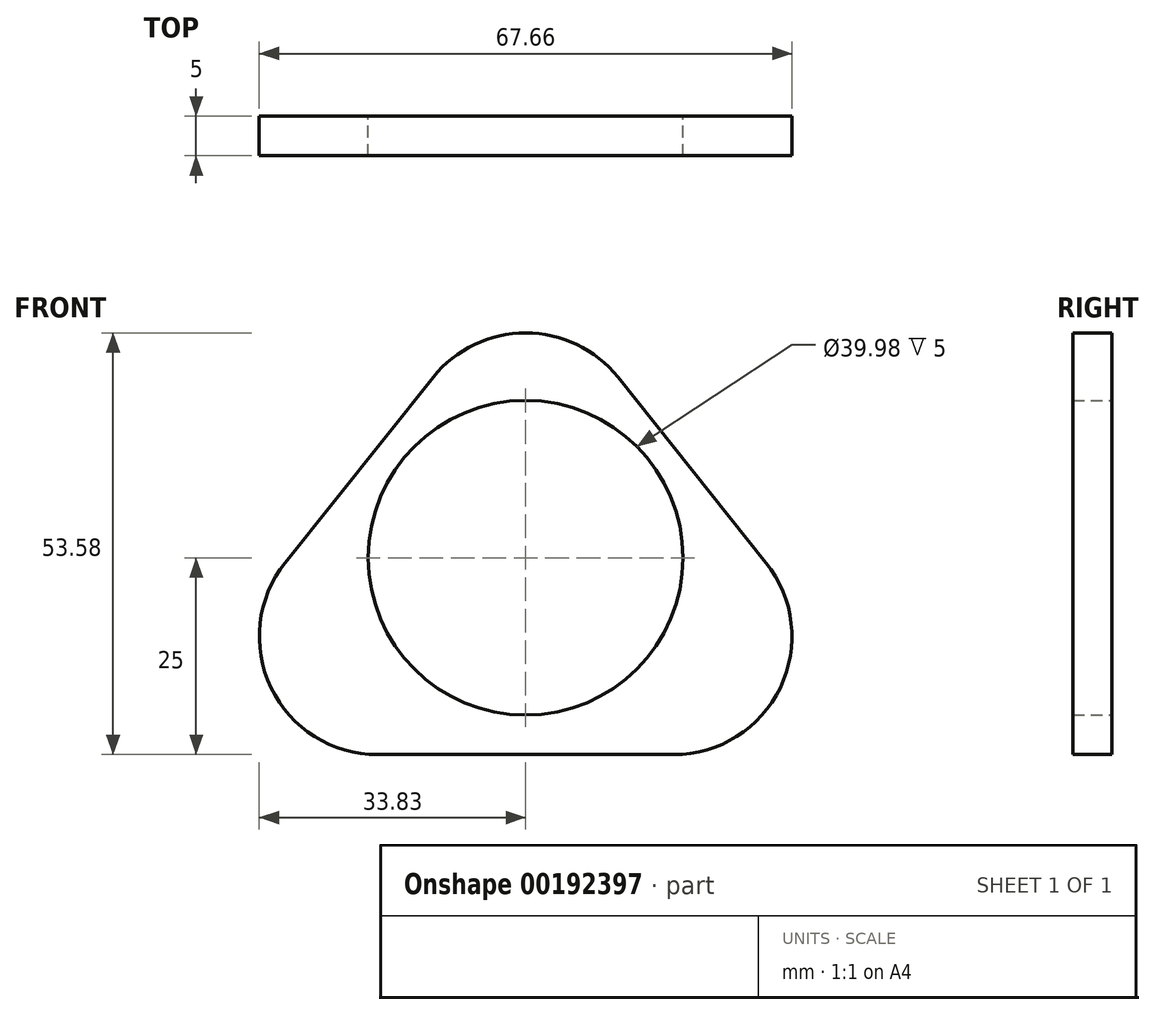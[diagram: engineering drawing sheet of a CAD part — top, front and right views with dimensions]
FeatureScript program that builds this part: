
annotation { "Feature Type Name" : "Feature", "Feature Type Description" : "" }
export const myFeature = defineFeature(function(context is Context, id is Id, definition is map)
    precondition{}
    {
        {
            var Q0;
            Q0=qCreatedBy(makeId("Front.planeOp"),FACE);
            var sketch = newSketch(context, id + "F0", { "sketchPlane" : qUnion([Q0])});
            skCircle(sketch, "E0", {"center": v(0, 0) * mm, "radius": 19.99 * mm});
            skLineSegment(sketch, "E1", {"start": v(0, -25) * mm, "end": v(-50, -25) * mm});
            skLineSegment(sketch, "E2", {"start": v(-50, -25) * mm, "end": v(0, 37.62) * mm});
            skLineSegment(sketch, "E3.MirrorCS", {"start": v(50, -25) * mm, "end": v(0, 37.62) * mm});
            skLineSegment(sketch, "E4.MirrorCS", {"start": v(0, -25) * mm, "end": v(50, -25) * mm});
            skSolve(sketch);
        }
        {
            var Q0;
            Q0 = qSketchRegion(id + "F0", true);
            extrude(context, id + "F1", {"entities" : qUnion([Q0]), "depth" : 5 * mm});
        }
        {
            var Q0;
            Q0=makeQuery(id+"F1.opExtrude","SWEPT_EDGE",EDGE,{"disambiguationData":[OSD([sQuery(id+"F0.wireOp",EDGE,"E2"),sQuery(id+"F0.wireOp",EDGE,"E3.MirrorCS")])]});
            var Q1;
            Q1=makeQuery(id+"F1.opExtrude","SWEPT_EDGE",EDGE,{"disambiguationData":[OSD([sQuery(id+"F0.wireOp",EDGE,"E1"),sQuery(id+"F0.wireOp",EDGE,"E2")])]});
            var Q2;
            Q2=makeQuery(id+"F1.opExtrude","SWEPT_EDGE",EDGE,{"disambiguationData":[OSD([sQuery(id+"F0.wireOp",EDGE,"E3.MirrorCS"),sQuery(id+"F0.wireOp",EDGE,"E4.MirrorCS")])]});
            fillet(context, id + "F2", {"entities" : qUnion([Q0, Q1, Q2]), "radius" : 15 * mm, "tangentPropagation" : true, "allowEdgeOverflow" : false});
        }
    });
